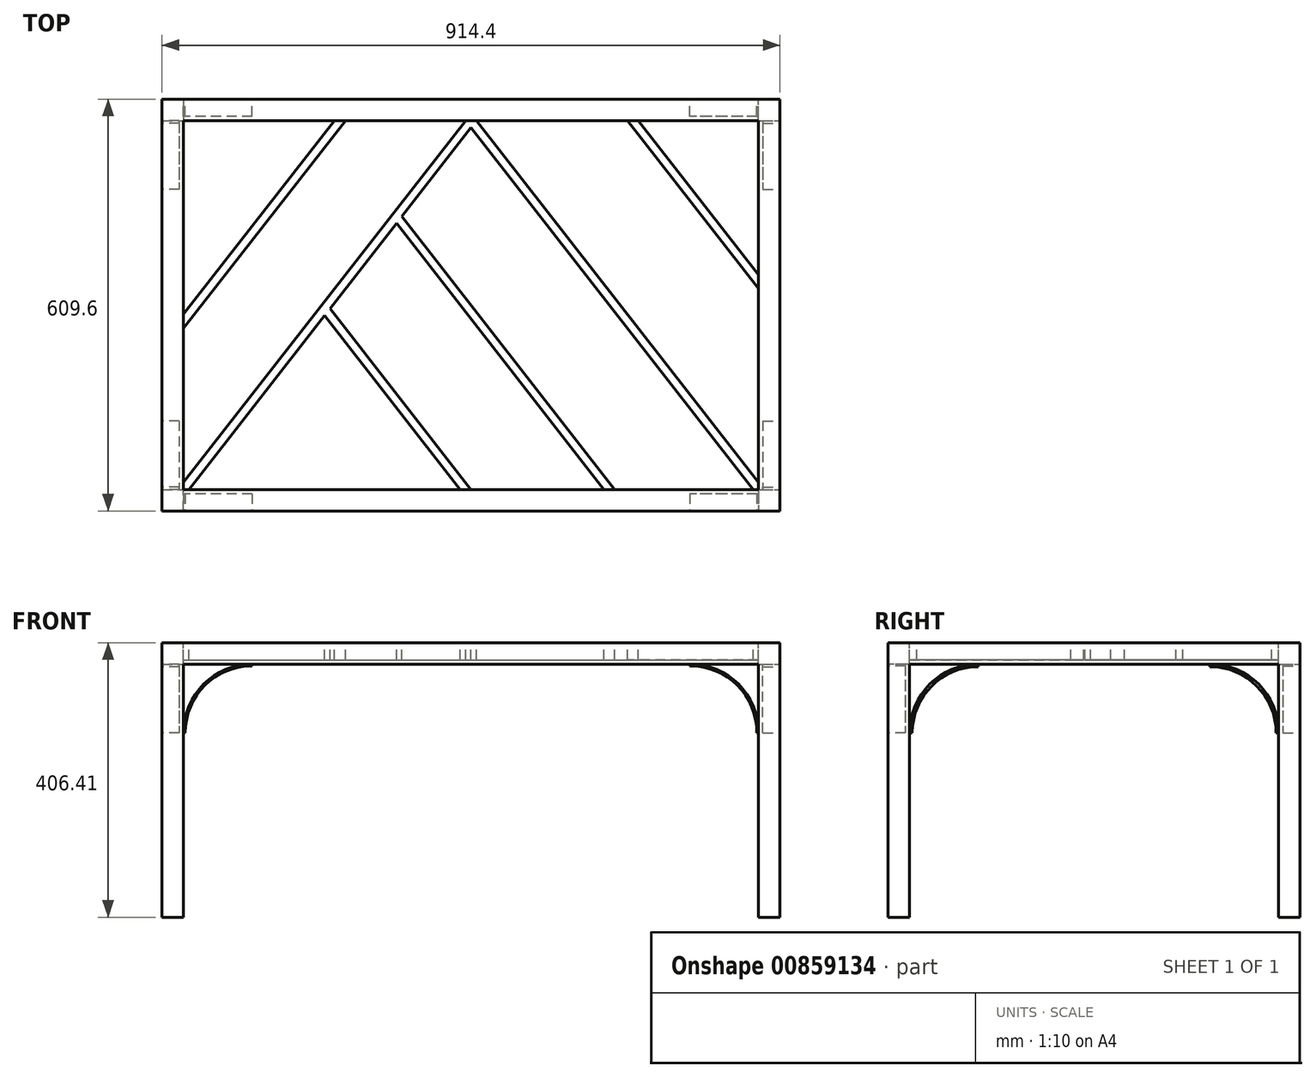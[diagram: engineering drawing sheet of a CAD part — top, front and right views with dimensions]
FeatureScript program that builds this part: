
annotation { "Feature Type Name" : "Feature", "Feature Type Description" : "" }
export const myFeature = defineFeature(function(context is Context, id is Id, definition is map)
    precondition{}
    {
        {
            var Q0;
            Q0=qCreatedBy(makeId("Top.planeOp"),FACE);
            var sketch = newSketch(context, id + "F0", { "sketchPlane" : qUnion([Q0])});
            skLineSegment(sketch, "E0.bottom", {"start": v(-457.2, 304.8) * mm, "end": v(457.2, 304.8) * mm});
            skLineSegment(sketch, "E0.top", {"start": v(-457.2, -304.8) * mm, "end": v(457.2, -304.8) * mm});
            skLineSegment(sketch, "E0.left", {"start": v(-457.2, 304.8) * mm, "end": v(-457.2, -304.8) * mm});
            skLineSegment(sketch, "E0.right", {"start": v(457.2, 304.8) * mm, "end": v(457.2, -304.8) * mm});
            skSolve(sketch);
        }
        {
            var Q0;
            Q0=makeQuery(id+"F0.imprint","IMPRINT",FACE,{"disambiguationData":[TD([[makeQuery(id+"F0.imprint","IMPRINT",EDGE,{"derivedFrom":sQuery(id+"F0.wireOp",EDGE,"E0.bottom")}),-1.0]])]});
            var Q1;
            Q1 = qSketchRegion(id + "F2", true);
            extrude(context, id + "F1", {"entities" : qUnion([Q0, Q1]), "endBound" : BoundingType.SYMMETRIC, "depth" : 31.75 * mm, "offsetDistance" : 25.4 * mm});
        }
        {
            var Q0;
            Q0=makeQuery(id+"F1.opExtrude","CAP_FACE",FACE,{"disambiguationData":[OSD([sQuery(id+"F0.wireOp",EDGE,"E0.bottom"),sQuery(id+"F0.wireOp",EDGE,"E0.top"),sQuery(id+"F0.wireOp",EDGE,"E0.left"),sQuery(id+"F0.wireOp",EDGE,"E0.right")])],"isStart":false});
            var sketch = newSketch(context, id + "F2", { "sketchPlane" : qUnion([Q0])});
            skLineSegment(sketch, "E1.bottom", {"start": v(-425.45, 273.05) * mm, "end": v(425.45, 273.05) * mm});
            skLineSegment(sketch, "E1.top", {"start": v(-425.45, -273.05) * mm, "end": v(425.45, -273.05) * mm});
            skLineSegment(sketch, "E1.left", {"start": v(-425.45, 273.05) * mm, "end": v(-425.45, -273.05) * mm});
            skLineSegment(sketch, "E1.right", {"start": v(425.45, 273.05) * mm, "end": v(425.45, -273.05) * mm});
            skSolve(sketch);
        }
        {
            var Q0;
            Q0 = qSketchRegion(id + "F2", true);
            extrude(context, id + "F3", {"entities" : qUnion([Q0]), "operationType" : NewBodyOperationType.REMOVE, "endBound" : BoundingType.THROUGH_ALL, "oppositeDirection" : true, "depth" : 25.4 * mm, "offsetDistance" : 25.4 * mm});
        }
        {
            var Q0;
            Q0=makeQuery(id+"F1.opExtrude","CAP_FACE",FACE,{"disambiguationData":[OSD([sQuery(id+"F0.wireOp",EDGE,"E0.bottom"),sQuery(id+"F0.wireOp",EDGE,"E0.top"),sQuery(id+"F0.wireOp",EDGE,"E0.left"),sQuery(id+"F0.wireOp",EDGE,"E0.right")])],"isStart":false});
            var sketch = newSketch(context, id + "F4", { "sketchPlane" : qUnion([Q0])});
            skLineSegment(sketch, "E2", {"start": v(0, 273.05) * mm, "end": v(0, -273.05) * mm, "construction": true});
            skLineSegment(sketch, "E3", {"start": v(-425.45, 0) * mm, "end": v(425.45, 0) * mm, "construction": true});
            skLineSegment(sketch, "E4", {"start": v(-425.45, -273.05) * mm, "end": v(0, 273.05) * mm, "construction": true});
            skLineSegment(sketch, "E5", {"start": v(-425.45, -262.72) * mm, "end": v(-8.05, 273.05) * mm});
            skLineSegment(sketch, "E6", {"start": v(-417.4, -273.05) * mm, "end": v(0, 262.72) * mm});
            skLineSegment(sketch, "E7", {"start": v(0, 273.05) * mm, "end": v(425.45, -273.05) * mm, "construction": true});
            skLineSegment(sketch, "E8", {"start": v(8.05, 273.05) * mm, "end": v(425.45, -262.72) * mm});
            skLineSegment(sketch, "E9", {"start": v(425.45, 24.16) * mm, "end": v(231.55, 273.05) * mm});
            skLineSegment(sketch, "E10", {"start": v(425.45, 44.83) * mm, "end": v(247.65, 273.05) * mm});
            skLineSegment(sketch, "E11", {"start": v(-8.05, 273.05) * mm, "end": v(8.05, 273.05) * mm});
            skLineSegment(sketch, "E12", {"start": v(231.55, 273.05) * mm, "end": v(247.65, 273.05) * mm});
            skLineSegment(sketch, "E13", {"start": v(425.45, 24.16) * mm, "end": v(425.45, 44.83) * mm});
            skLineSegment(sketch, "E14", {"start": v(417.4, -273.05) * mm, "end": v(425.45, -273.05) * mm});
            skLineSegment(sketch, "E15", {"start": v(425.45, -262.72) * mm, "end": v(425.45, -273.05) * mm});
            skLineSegment(sketch, "E16", {"start": v(-425.45, -262.72) * mm, "end": v(-425.45, -273.05) * mm});
            skLineSegment(sketch, "E17", {"start": v(-425.45, -273.05) * mm, "end": v(-417.4, -273.05) * mm});
            skLineSegment(sketch, "E18", {"start": v(-8.05, 273.05) * mm, "end": v(417.4, -273.05) * mm});
            skLineSegment(sketch, "E19", {"start": v(-102.34, 131.36) * mm, "end": v(212.73, -273.05) * mm});
            skLineSegment(sketch, "E20", {"start": v(-110.39, 121.03) * mm, "end": v(196.63, -273.05) * mm});
            skPoint(sketch, "E21.startSnap0", {"position": v(-212.73, 0) * mm});
            skLineSegment(sketch, "E22", {"start": v(-216.75, -15.5) * mm, "end": v(-16.1, -273.05) * mm});
            skLineSegment(sketch, "E23", {"start": v(-208.7, -5.17) * mm, "end": v(0, -273.05) * mm});
            skPoint(sketch, "E24", {"position": v(0, 0) * mm});
            skLineSegment(sketch, "E25", {"start": v(-216.75, -15.5) * mm, "end": v(-208.7, -5.17) * mm});
            skLineSegment(sketch, "E26", {"start": v(-16.1, -273.05) * mm, "end": v(0, -273.05) * mm});
            skLineSegment(sketch, "E27", {"start": v(212.73, -273.05) * mm, "end": v(196.63, -273.05) * mm});
            skLineSegment(sketch, "E28", {"start": v(-110.39, 121.03) * mm, "end": v(-102.34, 131.36) * mm});
            skLineSegment(sketch, "E29", {"start": v(-425.45, -34.5) * mm, "end": v(-185.85, 273.05) * mm});
            skLineSegment(sketch, "E30", {"start": v(-425.45, -34.5) * mm, "end": v(-425.45, -13.83) * mm});
            skLineSegment(sketch, "E31", {"start": v(-425.45, -13.83) * mm, "end": v(-201.95, 273.05) * mm});
            skLineSegment(sketch, "E32", {"start": v(-201.95, 273.05) * mm, "end": v(-185.85, 273.05) * mm});
            skSolve(sketch);
        }
        {
            var Q0;
            Q0 = qSketchRegion(id + "F4", true);
            extrude(context, id + "F5", {"entities" : qUnion([Q0]), "oppositeDirection" : true, "depth" : 25.4 * mm, "offsetDistance" : 25.4 * mm});
        }
        {
            var Q0;
            Q0=makeQuery(id+"F1.opExtrude","CAP_FACE",FACE,{"disambiguationData":[OSD([sQuery(id+"F0.wireOp",EDGE,"E0.bottom"),sQuery(id+"F0.wireOp",EDGE,"E0.top"),sQuery(id+"F0.wireOp",EDGE,"E0.left"),sQuery(id+"F0.wireOp",EDGE,"E0.right")])],"isStart":true});
            var sketch = newSketch(context, id + "F6", { "sketchPlane" : qUnion([Q0])});
            skLineSegment(sketch, "E33.bottom", {"start": v(-457.2, 304.8) * mm, "end": v(-425.45, 304.8) * mm});
            skLineSegment(sketch, "E33.top", {"start": v(-457.2, 273.05) * mm, "end": v(-425.45, 273.05) * mm});
            skLineSegment(sketch, "E33.left", {"start": v(-457.2, 304.8) * mm, "end": v(-457.2, 273.05) * mm});
            skLineSegment(sketch, "E33.right", {"start": v(-425.45, 304.8) * mm, "end": v(-425.45, 273.05) * mm});
            skLineSegment(sketch, "E34.bottom", {"start": v(-457.2, -304.8) * mm, "end": v(-425.45, -304.8) * mm});
            skLineSegment(sketch, "E34.top", {"start": v(-457.2, -273.05) * mm, "end": v(-425.45, -273.05) * mm});
            skLineSegment(sketch, "E34.left", {"start": v(-457.2, -304.8) * mm, "end": v(-457.2, -273.05) * mm});
            skLineSegment(sketch, "E34.right", {"start": v(-425.45, -304.8) * mm, "end": v(-425.45, -273.05) * mm});
            skLineSegment(sketch, "E35.bottom", {"start": v(425.45, 273.05) * mm, "end": v(457.2, 273.05) * mm});
            skLineSegment(sketch, "E35.top", {"start": v(425.45, 304.8) * mm, "end": v(457.2, 304.8) * mm});
            skLineSegment(sketch, "E35.left", {"start": v(425.45, 273.05) * mm, "end": v(425.45, 304.8) * mm});
            skLineSegment(sketch, "E35.right", {"start": v(457.2, 273.05) * mm, "end": v(457.2, 304.8) * mm});
            skLineSegment(sketch, "E36.bottom", {"start": v(425.45, -273.05) * mm, "end": v(457.2, -273.05) * mm});
            skLineSegment(sketch, "E36.top", {"start": v(425.45, -304.8) * mm, "end": v(457.2, -304.8) * mm});
            skLineSegment(sketch, "E36.left", {"start": v(425.45, -273.05) * mm, "end": v(425.45, -304.8) * mm});
            skLineSegment(sketch, "E36.right", {"start": v(457.2, -273.05) * mm, "end": v(457.2, -304.8) * mm});
            skSolve(sketch);
        }
        {
            var Q0;
            Q0 = qSketchRegion(id + "F6", true);
            extrude(context, id + "F7", {"entities" : qUnion([Q0]), "operationType" : NewBodyOperationType.ADD, "depth" : 374.65 * mm, "offsetDistance" : 25.4 * mm});
        }
        {
            var Q0;
            Q0=makeQuery(id+"F7.boolean.opBoolean","MERGE",FACE,{"derivedFrom":[makeQuery(id+"F1.opExtrude","SWEPT_FACE",FACE,{"disambiguationData":[OSD([sQuery(id+"F0.wireOp",EDGE,"E0.top")])]}),makeQuery(id+"F7.opExtrude","SWEPT_FACE",FACE,{"disambiguationData":[OSD([sQuery(id+"F6.wireOp",EDGE,"E33.bottom")])]}),makeQuery(id+"F7.opExtrude","SWEPT_FACE",FACE,{"disambiguationData":[OSD([sQuery(id+"F6.wireOp",EDGE,"E35.top")])]})]});
            var sketch = newSketch(context, id + "F8", { "sketchPlane" : qUnion([Q0])});
            skArc(sketch, "E37", {"start": v(-323.85, -15.88) * mm, "mid": v(-395.7, -45.63) * mm, "end": v(-425.45, -117.48) * mm});
            skArc(sketch, "E38.0", {"start": v(-323.85, -18.41) * mm, "mid": v(-393.9, -47.43) * mm, "end": v(-422.91, -117.48) * mm});
            skLineSegment(sketch, "E39", {"start": v(-422.91, -117.48) * mm, "end": v(-425.45, -117.48) * mm});
            skLineSegment(sketch, "E40", {"start": v(-323.85, -15.88) * mm, "end": v(-323.85, -18.41) * mm});
            skLineSegment(sketch, "E41", {"start": v(0, 0) * mm, "end": v(0, -406.78) * mm});
            skArc(sketch, "E42.MirrorCS", {"start": v(323.85, -18.41) * mm, "mid": v(393.9, -47.43) * mm, "end": v(422.91, -117.47) * mm});
            skArc(sketch, "E43.MirrorCS", {"start": v(323.85, -15.87) * mm, "mid": v(395.7, -45.63) * mm, "end": v(425.45, -117.47) * mm});
            skLineSegment(sketch, "E44.MirrorCS", {"start": v(323.85, -15.87) * mm, "end": v(323.85, -18.41) * mm});
            skLineSegment(sketch, "E45.MirrorCS", {"start": v(422.91, -117.47) * mm, "end": v(425.45, -117.47) * mm});
            skSolve(sketch);
        }
        {
            var Q0;
            Q0 = qSketchRegion(id + "F8", true);
            extrude(context, id + "F9", {"entities" : qUnion([Q0]), "oppositeDirection" : true, "depth" : 25.4 * mm, "offsetDistance" : 25.4 * mm});
        }
        {
            var Q0;
            Q0=makeQuery(id+"F9.opExtrude","SWEPT_BODY",BODY,{"disambiguationData":[OSD([sQuery(id+"F8.wireOp",EDGE,"E37"),sQuery(id+"F8.wireOp",EDGE,"E38.0"),sQuery(id+"F8.wireOp",EDGE,"E39"),sQuery(id+"F8.wireOp",EDGE,"E40")])]});
            var Q1;
            Q1=makeQuery(id+"F9.opExtrude","SWEPT_BODY",BODY,{"disambiguationData":[OSD([sQuery(id+"F8.wireOp",EDGE,"E42.MirrorCS"),sQuery(id+"F8.wireOp",EDGE,"E43.MirrorCS"),sQuery(id+"F8.wireOp",EDGE,"E44.MirrorCS"),sQuery(id+"F8.wireOp",EDGE,"E45.MirrorCS")])]});
            var Q2;
            Q2=qCreatedBy(makeId("Front.planeOp"),FACE);
            mirror(context, id + "F10", {"entities" : qUnion([Q0, Q1]), "mirrorPlane" : qUnion([Q2])});
        }
        {
            var Q0;
            Q0=makeQuery(id+"F7.boolean.opBoolean","MERGE",FACE,{"derivedFrom":[makeQuery(id+"F1.opExtrude","SWEPT_FACE",FACE,{"disambiguationData":[OSD([sQuery(id+"F0.wireOp",EDGE,"E0.right")])]}),makeQuery(id+"F7.opExtrude","SWEPT_FACE",FACE,{"disambiguationData":[OSD([sQuery(id+"F6.wireOp",EDGE,"E35.right")])]}),makeQuery(id+"F7.opExtrude","SWEPT_FACE",FACE,{"disambiguationData":[OSD([sQuery(id+"F6.wireOp",EDGE,"E36.right")])]})]});
            var sketch = newSketch(context, id + "F11", { "sketchPlane" : qUnion([Q0])});
            skArc(sketch, "E46", {"start": v(171.45, -15.88) * mm, "mid": v(243.3, -45.63) * mm, "end": v(273.05, -117.48) * mm});
            skArc(sketch, "E47.0", {"start": v(171.45, -19.69) * mm, "mid": v(240.6, -48.33) * mm, "end": v(269.24, -117.47) * mm});
            skLineSegment(sketch, "E48", {"start": v(273.05, -117.47) * mm, "end": v(269.24, -117.47) * mm});
            skLineSegment(sketch, "E49", {"start": v(171.45, -19.68) * mm, "end": v(171.45, -15.88) * mm});
            skLineSegment(sketch, "E50", {"start": v(0, 0) * mm, "end": v(0, -326.53) * mm, "construction": true});
            skArc(sketch, "E51.MirrorCS", {"start": v(-171.45, -19.69) * mm, "mid": v(-240.6, -48.33) * mm, "end": v(-269.24, -117.48) * mm});
            skArc(sketch, "E52.MirrorCS", {"start": v(-171.45, -15.88) * mm, "mid": v(-243.3, -45.63) * mm, "end": v(-273.05, -117.48) * mm});
            skLineSegment(sketch, "E53.MirrorCS", {"start": v(-273.05, -117.48) * mm, "end": v(-269.24, -117.48) * mm});
            skLineSegment(sketch, "E54.MirrorCS", {"start": v(-171.45, -19.69) * mm, "end": v(-171.45, -15.88) * mm});
            skSolve(sketch);
        }
        {
            var Q0;
            Q0 = qSketchRegion(id + "F11", true);
            extrude(context, id + "F12", {"entities" : qUnion([Q0]), "oppositeDirection" : true, "depth" : 25.4 * mm, "offsetDistance" : 25.4 * mm});
        }
        {
            var Q0;
            Q0=makeQuery(id+"F12.opExtrude","SWEPT_BODY",BODY,{"disambiguationData":[OSD([sQuery(id+"F11.wireOp",EDGE,"E51.MirrorCS"),sQuery(id+"F11.wireOp",EDGE,"E52.MirrorCS"),sQuery(id+"F11.wireOp",EDGE,"E53.MirrorCS"),sQuery(id+"F11.wireOp",EDGE,"E54.MirrorCS")])]});
            var Q1;
            Q1=makeQuery(id+"F12.opExtrude","SWEPT_BODY",BODY,{"disambiguationData":[OSD([sQuery(id+"F11.wireOp",EDGE,"E46"),sQuery(id+"F11.wireOp",EDGE,"E47.0"),sQuery(id+"F11.wireOp",EDGE,"E48"),sQuery(id+"F11.wireOp",EDGE,"E49")])]});
            var Q2;
            Q2=qCreatedBy(makeId("Right.planeOp"),FACE);
            mirror(context, id + "F13", {"entities" : qUnion([Q0, Q1]), "mirrorPlane" : qUnion([Q2])});
        }
        {
            var Q0;
            Q0=qCreatedBy(makeId("Top.planeOp"),FACE);
            cPlane(context, id + "F14", {"entities" : qUnion([Q0]), "cplaneType" : CPlaneType.OFFSET, "offset" : 279.4 * mm, "oppositeDirection" : true, "width" : 152.4 * mm, "height" : 152.4 * mm});
        }
    });
